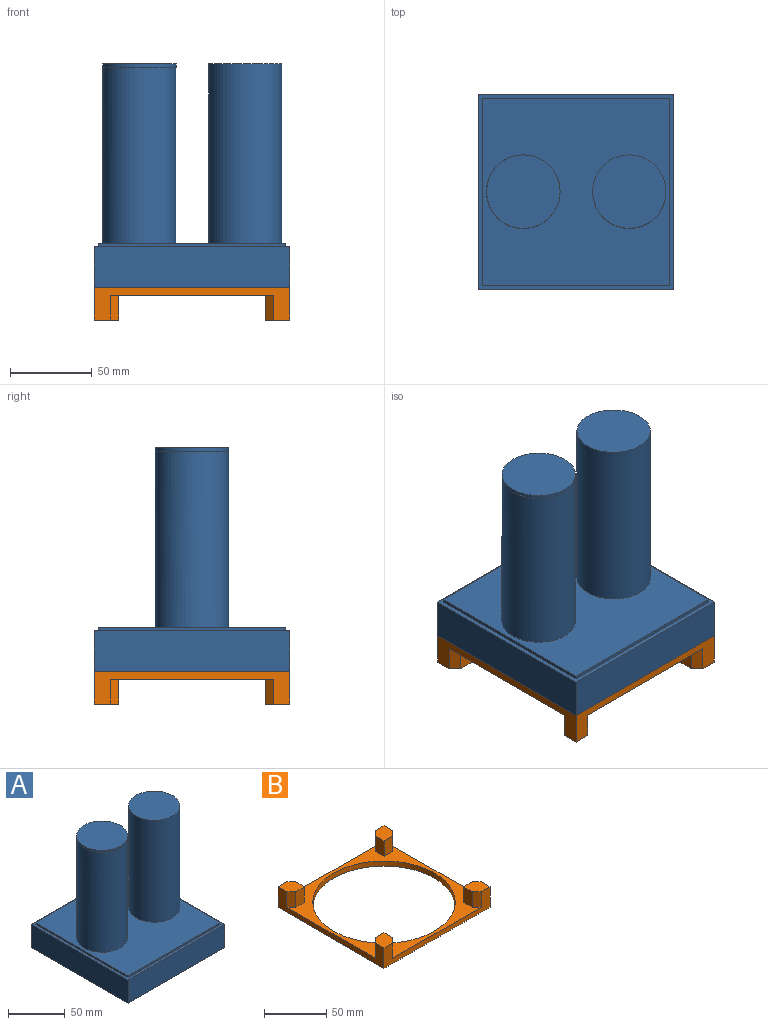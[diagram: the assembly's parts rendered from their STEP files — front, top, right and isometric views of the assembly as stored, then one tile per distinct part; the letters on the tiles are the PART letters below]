
ASSEMBLY  parts=2 mates=1
PART A: 24 faces, bbox 120x120x137 mm
  f0: plane 120x120mm, normal (0,0,1), area 1175mm2, adj f1,f2,f3,f5,f7,f8,f9,f10
  f1: plane 120x25mm, normal (0,-1,0), area 3000mm2, adj f0,f2,f5,f6
  f2: plane 120x25mm, normal (1,0,0), area 3000mm2, adj f0,f1,f3,f6
  f3: plane 120x25mm, normal (0,1,0), area 3000mm2, adj f0,f2,f5,f6
  f4: cylinder r=57mm len=114mm, axis (0,0,1), area 8953.5mm2, adj f6,f12
  f5: plane 120x25mm, normal (-1,0,0), area 3000mm2, adj f0,f1,f3,f6
  f6: plane 120x120mm, normal (0,0,-1), area 4193mm2, adj f1,f2,f3,f4,f5
  f7: plane 115x2mm, normal (0,-1,0), area 230mm2, adj f0,f8,f10,f11
  f8: plane 115x2mm, normal (1,0,0), area 230mm2, adj f0,f7,f9,f11
  f9: plane 115x2mm, normal (0,1,0), area 230mm2, adj f0,f8,f10,f11
  f10: plane 115x2mm, normal (-1,0,0), area 230mm2, adj f0,f7,f9,f11
  f11: plane 115x115mm, normal (0,0,1), area 10044.1mm2, adj f7,f8,f9,f10,f14,f17
  f12: plane 114x114mm, normal (0,0,-1), area 7693.8mm2, adj f4,f13,f16
  f13: cylinder r=20mm len=110mm, axis (0,0,-1), area 13823mm2, adj f12,f21
  f14: cylinder r=22.5mm len=108mm, axis (0,0,-1), area 15268.1mm2, adj f11,f15,f20
  f15: plane 45x22.55mm, normal (0,0,1), area 4.8mm2, adj f14,f19
  f16: cylinder r=20mm len=110mm, axis (0,0,-1), area 13823mm2, adj f12,f22
  f17: cylinder r=22.5mm len=110mm, axis (0,0,-1), area 15550.9mm2, adj f11,f23
  f18: plane 45x45mm, normal (0,0,1), area 1590.4mm2, adj f19
  f19: cylinder r=22.5mm len=45mm, axis (0,0,-1), area 282.7mm2, adj f15,f18,f20
  f20: plane 45x22.55mm, normal (0,0,-1), area 4.8mm2, adj f14,f19
  f21: plane 40x40mm, normal (0,0,-1), area 1256.6mm2, adj f13
  f22: plane 40x40mm, normal (0,0,-1), area 1256.6mm2, adj f16
  f23: plane 45x45mm, normal (0,0,1), area 1590.4mm2, adj f17
PART B: 27 faces, bbox 120x120x20 mm
  f0: plane 120x20mm, normal (0,1,0), area 900mm2, adj f1,f3,f5,f6,f15,f18,f19,f22
  f1: plane 120x20mm, normal (-1,0,0), area 900mm2, adj f0,f2,f5,f6,f12,f18,f20,f26
  f2: plane 120x20mm, normal (0,-1,0), area 900mm2, adj f1,f3,f5,f6,f9,f12,f24,f25
  f3: plane 120x20mm, normal (1,0,0), area 900mm2, adj f0,f2,f5,f6,f9,f15,f21,f23
  f4: cylinder r=57mm len=114mm, axis (0,0,-1), area 1790.7mm2, adj f5,f6
  f5: plane 120x120mm, normal (0,0,1), area 3393mm2, adj f0,f1,f2,f3,f4,f7,f8,f10
  f6: plane 120x120mm, normal (0,0,-1), area 4193mm2, adj f0,f1,f2,f3,f4
  f7: plane 15x10mm, normal (0,1,0), area 150mm2, adj f5,f8,f9,f23
  f8: plane 15x10mm, normal (-1,0,0), area 150mm2, adj f5,f7,f9,f24
  f9: plane 15x15mm, normal (0,0,1), area 200mm2, adj f2,f3,f7,f8,f23,f24
  f10: plane 15x10mm, normal (0,1,0), area 150mm2, adj f5,f11,f12,f26
  f11: plane 15x10mm, normal (1,0,0), area 150mm2, adj f5,f10,f12,f25
  f12: plane 15x15mm, normal (0,0,1), area 200mm2, adj f1,f2,f10,f11,f25,f26
  f13: plane 15x10mm, normal (0,-1,0), area 150mm2, adj f5,f14,f15,f21
  f14: plane 15x10mm, normal (-1,0,0), area 150mm2, adj f5,f13,f15,f22
  f15: plane 15x15mm, normal (0,0,1), area 200mm2, adj f0,f3,f13,f14,f21,f22
  f16: plane 15x10mm, normal (0,-1,0), area 150mm2, adj f5,f17,f18,f20
  f17: plane 15x10mm, normal (1,0,0), area 150mm2, adj f5,f16,f18,f19
  f18: plane 15x15mm, normal (0,0,1), area 200mm2, adj f0,f1,f16,f17,f19,f20
  f19: plane 15x5mm, normal (0.71,0.71,0), area 106.1mm2, adj f0,f5,f17,f18
  f20: plane 15x5mm, normal (-0.71,-0.71,0), area 106.1mm2, adj f1,f5,f16,f18
  f21: plane 15x5mm, normal (0.71,-0.71,0), area 106.1mm2, adj f3,f5,f13,f15
  f22: plane 15x5mm, normal (-0.71,0.71,0), area 106.1mm2, adj f0,f5,f14,f15
  f23: plane 15x5mm, normal (0.71,0.71,0), area 106.1mm2, adj f3,f5,f7,f9
  f24: plane 15x5mm, normal (-0.71,-0.71,0), area 106.1mm2, adj f2,f5,f8,f9
  f25: plane 15x5mm, normal (0.71,-0.71,0), area 106.1mm2, adj f2,f5,f11,f12
  f26: plane 15x5mm, normal (-0.71,0.71,0), area 106.1mm2, adj f1,f5,f10,f12
PLACE A t=(0.34,-0.69,-45.1)mm fixed
PLACE B rot(axis=(0,1,0),180deg) t=(0.34,-0.69,-70.1)mm
MATE parallel B.f6 <-> A.f6  axis (0,0,1) through (-59.66,-60.69,-70.1)mm
